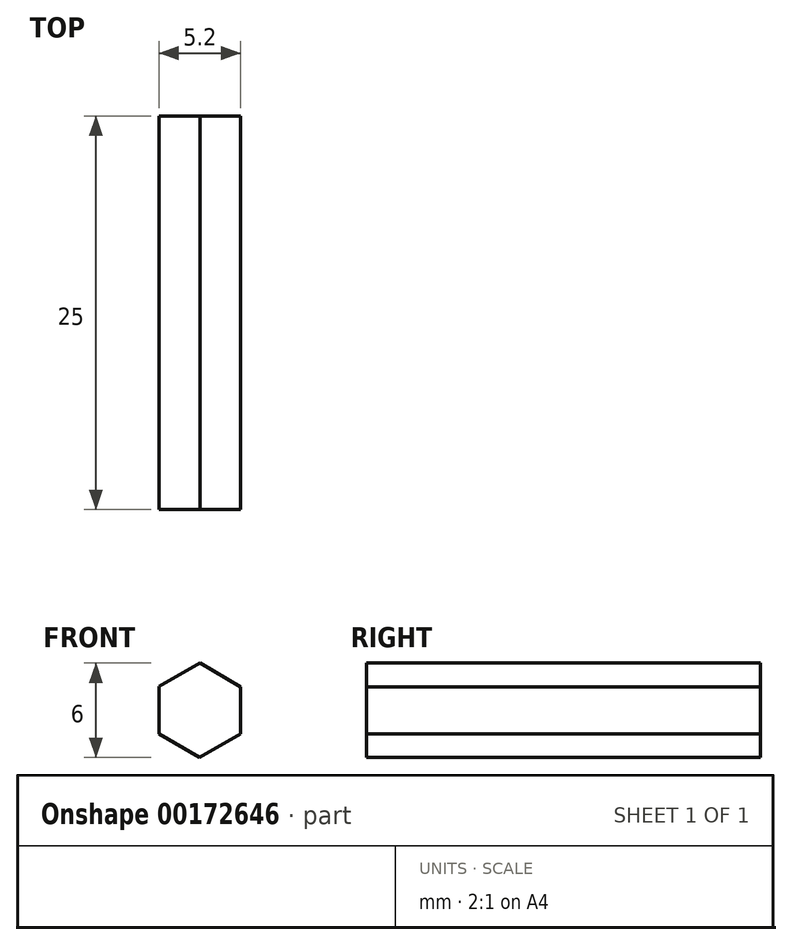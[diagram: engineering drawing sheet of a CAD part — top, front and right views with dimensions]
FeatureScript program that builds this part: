
annotation { "Feature Type Name" : "Feature", "Feature Type Description" : "" }
export const myFeature = defineFeature(function(context is Context, id is Id, definition is map)
    precondition{}
    {
        {
            var Q0;
            Q0=qCreatedBy(makeId("Front.planeOp"),FACE);
            var sketch = newSketch(context, id + "F0", { "sketchPlane" : qUnion([Q0])});
            skCircle(sketch, "E0.cCircle", {"center": v(0, 0) * mm, "radius": 2.6 * mm, "construction": true});
            skLineSegment(sketch, "E0.0", {"start": v(2.6, -1.5) * mm, "end": v(0, -3) * mm});
            skLineSegment(sketch, "E0.1", {"start": v(0, -3) * mm, "end": v(-2.6, -1.5) * mm});
            skLineSegment(sketch, "E0.2", {"start": v(-2.6, -1.5) * mm, "end": v(-2.6, 1.5) * mm});
            skLineSegment(sketch, "E0.3", {"start": v(-2.6, 1.5) * mm, "end": v(0, 3) * mm});
            skLineSegment(sketch, "E0.4", {"start": v(0, 3) * mm, "end": v(2.6, 1.5) * mm});
            skLineSegment(sketch, "E0.5", {"start": v(2.6, 1.5) * mm, "end": v(2.6, -1.5) * mm});
            skPoint(sketch, "E0.0.midPoint", {"position": v(1.3, -2.25) * mm});
            skSolve(sketch);
        }
        {
            var Q0;
            Q0=makeQuery(id+"F0.imprint","IMPRINT",FACE,{"disambiguationData":[TD([[makeQuery(id+"F0.imprint","IMPRINT",EDGE,{"derivedFrom":sQuery(id+"F0.wireOp",EDGE,"E0.0")}),-1.0]])]});
            extrude(context, id + "F1", {"entities" : qUnion([Q0]), "depth" : 25 * mm});
        }
    });
